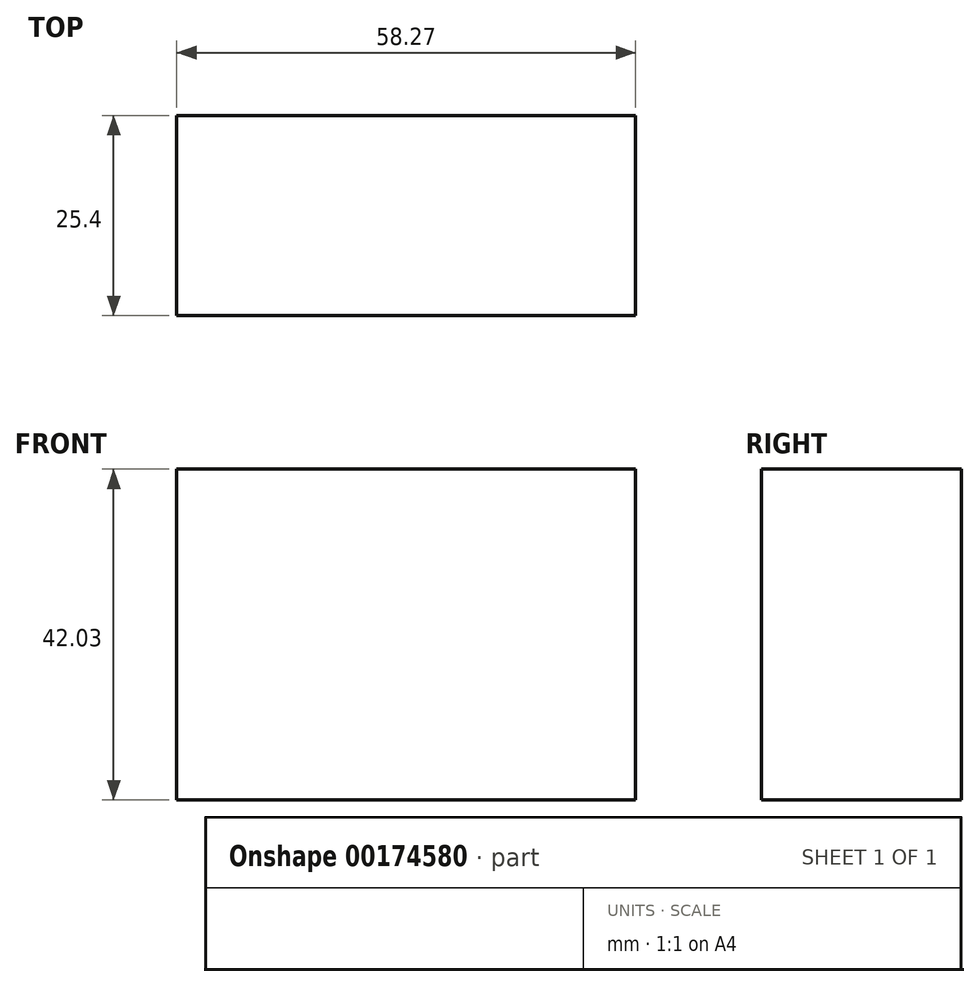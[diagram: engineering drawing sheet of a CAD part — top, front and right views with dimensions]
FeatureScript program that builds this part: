
annotation { "Feature Type Name" : "Feature", "Feature Type Description" : "" }
export const myFeature = defineFeature(function(context is Context, id is Id, definition is map)
    precondition{}
    {
        {
            var Q0;
            Q0=qCreatedBy(makeId("Front.planeOp"),FACE);
            var sketch = newSketch(context, id + "F0", { "sketchPlane" : qUnion([Q0])});
            skLineSegment(sketch, "E0.bottom", {"start": v(0, 0) * mm, "end": v(58.27, 0) * mm});
            skLineSegment(sketch, "E0.top", {"start": v(0, 42.03) * mm, "end": v(58.27, 42.03) * mm});
            skLineSegment(sketch, "E0.left", {"start": v(0, 0) * mm, "end": v(0, 42.03) * mm});
            skLineSegment(sketch, "E0.right", {"start": v(58.27, 0) * mm, "end": v(58.27, 42.03) * mm});
            skSolve(sketch);
        }
        {
            var Q0;
            Q0 = qSketchRegion(id + "F0", true);
            extrude(context, id + "F1", {"entities" : qUnion([Q0]), "depth" : 25.4 * mm});
        }
    });
